# Revit family: Ghent - Challenger Series - Floor Case Collection
name_source: partatom
category: Generic Models
units: mm (PartAtom-declared; Revit-internal decimal feet)

## family parameters
Always vertical = Yes
Can host rebar = No
Cut with Voids When Loaded = No
Part Type = Normal
Room Calculation Point = No
Round Connector Dimension = Use Diameter
Shared = No
Work Plane-Based = No

## types (15) — shared parameters
Frame = <By Category>
Glass = Glass, Clear Glazing, Tempered
Manufacturer = Ghent
URL = https://ghent.com

## per-type parameters (varying)
| type | 12 Shelve Position | 12 Shelves | 6 Shelves | Base | Door Width | Extended Base | Model | Shelf Width | Sweep Return Control | VH | Width |
| 104 – Floor Case with Wood-Grained Vinyl Base – 66" × 48" × 16" | 1' - 10 1/2" | No | Yes | Yes | 1' - 11" | No | 10404-XX-XX | 1' - 10" | 3' - 10 1/2" | 0' - 0 3/4" | 4' - 0" |
| 104 – Floor Case with Wood-Grained Vinyl Base – 66" × 60" × 16" | 2' - 4 1/2" | No | Yes | Yes | 2' - 5" | No | 10405-XX-XX | 2' - 4" | 4' - 10 1/2" | 0' - 0 3/4" | 5' - 0" |
| 104 – Floor Case with Wood-Grained Vinyl Base – 66" × 72" × 16" | 2' - 10 1/2" | No | Yes | Yes | 2' - 11" | No | 10406-XX-XX | 2' - 10" | 5' - 10 1/2" | 0' - 0 3/4" | 6' - 0" |
| 104 – Floor Case with Wood-Grained Vinyl Base – 66" × 96" × 16" | 1' - 10 1/2" | Yes | No | Yes | 1' - 11" | Yes | 10408-XX-XX | 1' - 10" | 3' - 11 3/8" | 6' - 0" | 8' - 0" |
| 104 – Floor Case with Wood-Grained Vinyl Base – 66" × 120" × 16" | 2' - 4 1/2" | Yes | No | Yes | 2' - 5" | Yes | 10410-XX-XX | 2' - 4" | 4' - 11 3/8" | 6' - 0" | 10' - 0" |
| 104 – Floor Case with Wood-Grained Vinyl Base – 66" × 144" × 16" | 2' - 10 1/2" | Yes | No | Yes | 2' - 11" | Yes | 10412-XX-XX | 2' - 10" | 5' - 11 3/8" | 6' - 0" | 12' - 0" |
| 134 – Floor Case with Black Laminate Base – 66" × 48" × 16" | 1' - 10 1/2" | No | Yes | Yes | 1' - 11" | No | 13404-XX-XX | 1' - 10" | 3' - 10 1/2" | 0' - 0 3/4" | 4' - 0" |
| 134 – Floor Case with Black Laminate Base – 66" × 60" × 16" | 2' - 4 1/2" | No | Yes | Yes | 2' - 5" | No | 13405-XX-XX | 2' - 4" | 4' - 10 1/2" | 0' - 0 3/4" | 5' - 0" |
| 134 – Floor Case with Black Laminate Base – 66" × 72" × 16" | 2' - 10 1/2" | No | Yes | Yes | 2' - 11" | No | 13406-XX-XX | 2' - 10" | 5' - 10 1/2" | 0' - 0 3/4" | 6' - 0" |
| 114 – Floor Case with Aluminum Legs – 66" × 48" × 16" | 1' - 10 1/2" | No | Yes | No | 1' - 11" | No | 11404-XX-XX | 1' - 10" | 3' - 10 1/2" | 0' - 0 3/4" | 4' - 0" |
| 114 – Floor Case with Aluminum Legs – 66" × 60" × 16" | 2' - 4 1/2" | No | Yes | No | 2' - 5" | No | 11405-XX-XX | 2' - 4" | 4' - 10 1/2" | 0' - 0 3/4" | 5' - 0" |
| 114 – Floor Case with Aluminum Legs – 66" × 72" × 16" | 2' - 10 1/2" | No | Yes | No | 2' - 11" | No | 11406-XX-XX | 2' - 10" | 5' - 10 1/2" | 0' - 0 3/4" | 6' - 0" |
| 114 – Floor Case with Aluminum Legs – 66" × 96" × 16" | 1' - 10 1/2" | Yes | No | No | 1' - 11" | No | 11408-XX-XX | 1' - 10" | 3' - 11 3/8" | 6' - 0" | 8' - 0" |
| 114 – Floor Case with Aluminum Legs – 66" × 120" × 16" | 2' - 4 1/2" | Yes | No | No | 2' - 5" | No | 11410-XX-XX | 2' - 4" | 4' - 11 3/8" | 6' - 0" | 10' - 0" |
| 114 – Floor Case with Aluminum Legs – 66" × 144" × 16" | 2' - 10 1/2" | Yes | No | No | 2' - 11" | No | 11412-XX-XX | 2' - 10" | 5' - 11 3/8" | 6' - 0" | 12' - 0" |

## geometry (parser evidence)
native form markers: Sweep x19
no freeform markers — native parametric forms only
